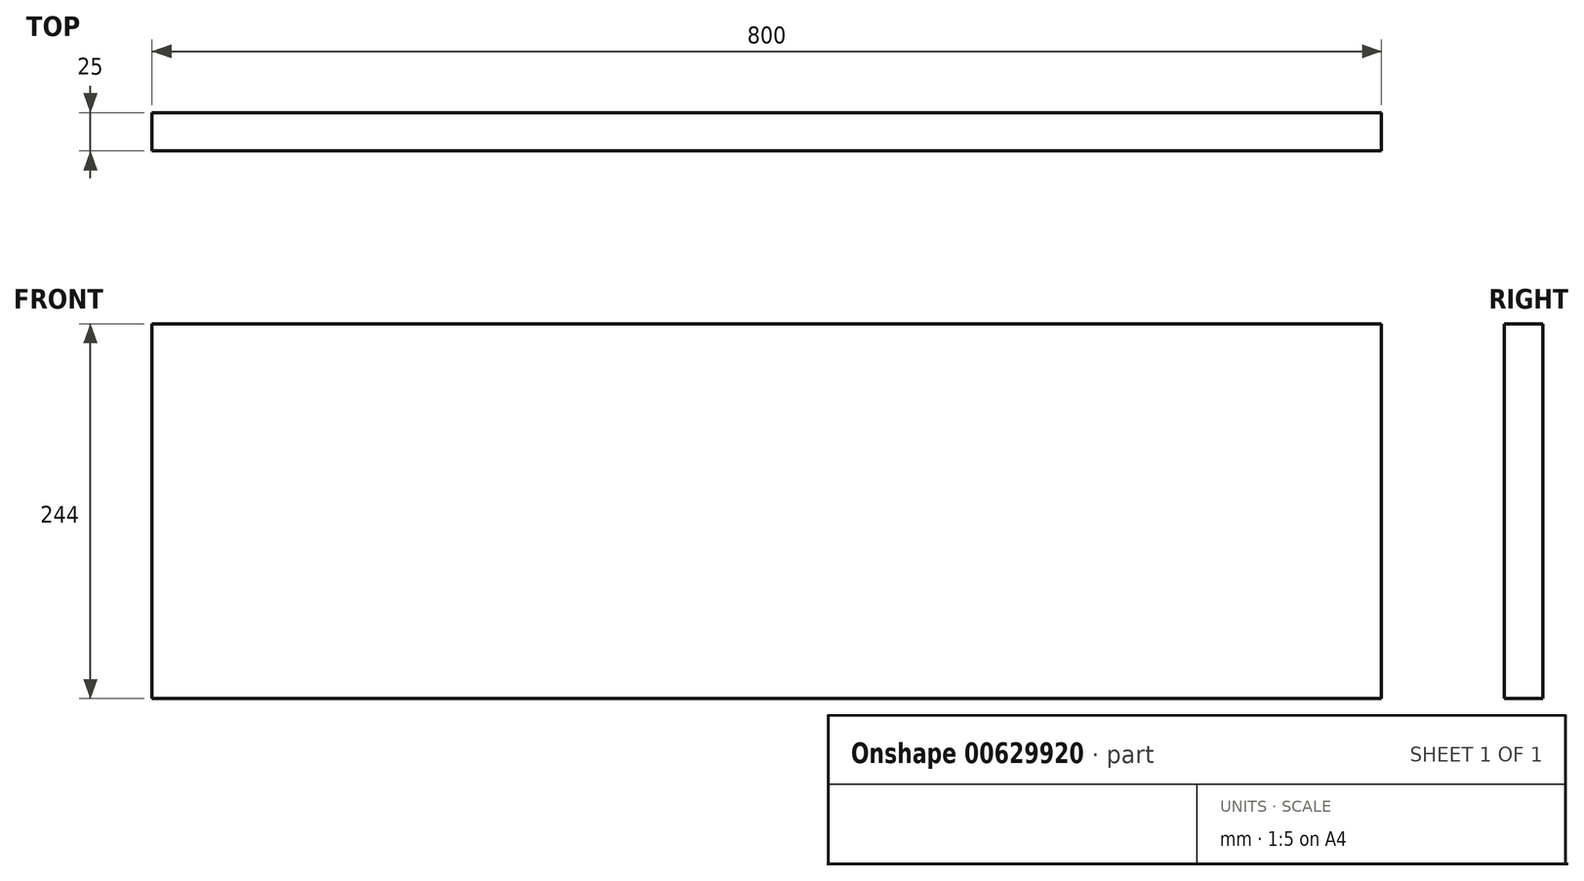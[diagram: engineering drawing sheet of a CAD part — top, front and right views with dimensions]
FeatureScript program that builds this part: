
annotation { "Feature Type Name" : "Feature", "Feature Type Description" : "" }
export const myFeature = defineFeature(function(context is Context, id is Id, definition is map)
    precondition{}
    {
        {
            var Q0;
            Q0=qCreatedBy(makeId("Front.planeOp"),FACE);
            var sketch = newSketch(context, id + "F0", { "sketchPlane" : qUnion([Q0])});
            skLineSegment(sketch, "E0.bottom", {"start": v(0, 0) * mm, "end": v(800, 0) * mm});
            skLineSegment(sketch, "E0.top", {"start": v(0, 244) * mm, "end": v(800, 244) * mm});
            skLineSegment(sketch, "E0.left", {"start": v(0, 0) * mm, "end": v(0, 244) * mm});
            skLineSegment(sketch, "E0.right", {"start": v(800, 0) * mm, "end": v(800, 244) * mm});
            skSolve(sketch);
        }
        {
            var Q0;
            Q0=makeQuery(id+"F0.imprint","IMPRINT",FACE,{"disambiguationData":[TD([[makeQuery(id+"F0.imprint","IMPRINT",EDGE,{"derivedFrom":sQuery(id+"F0.wireOp",EDGE,"E0.bottom")}),1.0]])]});
            extrude(context, id + "F1", {"entities" : qUnion([Q0]), "depth" : 25 * mm, "offsetDistance" : 25 * mm});
        }
    });
